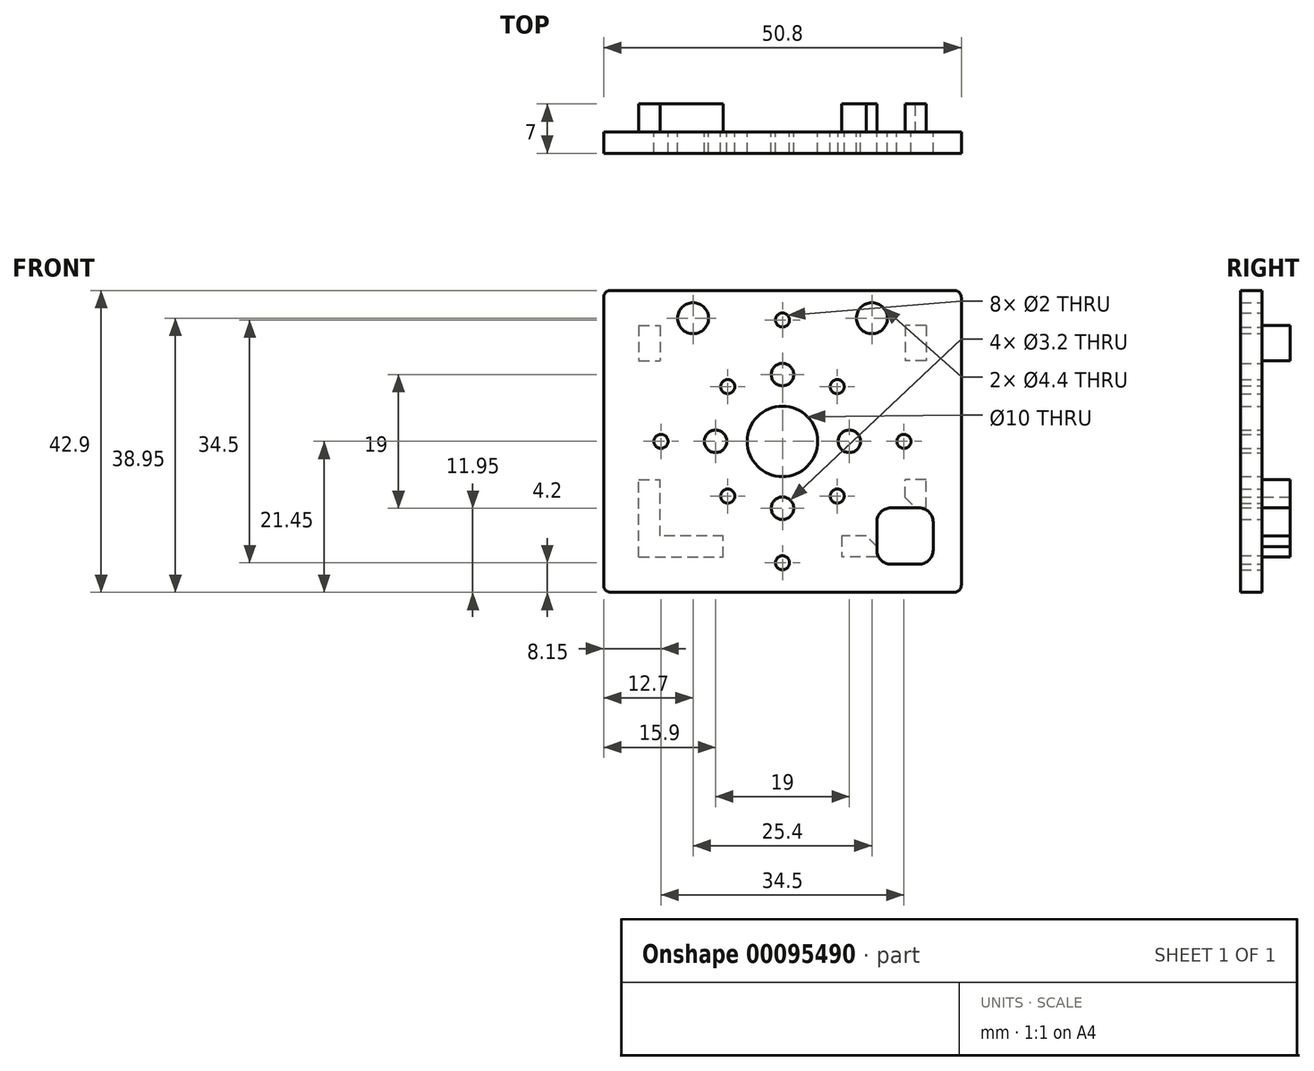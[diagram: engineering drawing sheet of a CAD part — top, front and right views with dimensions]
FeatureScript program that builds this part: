
annotation { "Feature Type Name" : "Feature", "Feature Type Description" : "" }
export const myFeature = defineFeature(function(context is Context, id is Id, definition is map)
    precondition{}
    {
        {
            var Q0;
            Q0=qCreatedBy(makeId("Front.planeOp"),FACE);
            var sketch = newSketch(context, id + "F0", { "sketchPlane" : qUnion([Q0])});
            skLineSegment(sketch, "E0.bottom", {"start": v(25.4, 21.45) * mm, "end": v(-25.4, 21.45) * mm});
            skLineSegment(sketch, "E0.top", {"start": v(25.4, -21.45) * mm, "end": v(-25.4, -21.45) * mm});
            skLineSegment(sketch, "E0.left", {"start": v(25.4, 21.45) * mm, "end": v(25.4, -21.45) * mm});
            skLineSegment(sketch, "E0.right", {"start": v(-25.4, 21.45) * mm, "end": v(-25.4, -21.45) * mm});
            skPoint(sketch, "E0.middle", {"position": v(0, 0) * mm});
            skCircle(sketch, "E1", {"center": v(0, 0) * mm, "radius": 5 * mm});
            skLineSegment(sketch, "E2.bottom", {"start": v(19.4, -17.45) * mm, "end": v(15.4, -17.45) * mm});
            skLineSegment(sketch, "E2.top", {"start": v(19.4, -9.45) * mm, "end": v(15.4, -9.45) * mm});
            skLineSegment(sketch, "E2.left", {"start": v(21.4, -15.45) * mm, "end": v(21.4, -11.45) * mm});
            skLineSegment(sketch, "E2.right", {"start": v(13.4, -15.45) * mm, "end": v(13.4, -11.45) * mm});
            skPoint(sketch, "E3.visualSharp", {"position": v(13.4, -9.45) * mm});
            skArc(sketch, "E3.filletArc", {"start": v(15.4, -9.45) * mm, "mid": v(13.99, -10.04) * mm, "end": v(13.4, -11.45) * mm});
            skPoint(sketch, "E4.visualSharp", {"position": v(21.4, -9.45) * mm});
            skArc(sketch, "E4.filletArc", {"start": v(21.4, -11.45) * mm, "mid": v(20.81, -10.04) * mm, "end": v(19.4, -9.45) * mm});
            skPoint(sketch, "E5.visualSharp", {"position": v(21.4, -17.45) * mm});
            skArc(sketch, "E5.filletArc", {"start": v(19.4, -17.45) * mm, "mid": v(20.81, -16.86) * mm, "end": v(21.4, -15.45) * mm});
            skPoint(sketch, "E6.visualSharp", {"position": v(13.4, -17.45) * mm});
            skArc(sketch, "E6.filletArc", {"start": v(13.4, -15.45) * mm, "mid": v(13.99, -16.86) * mm, "end": v(15.4, -17.45) * mm});
            skCircle(sketch, "E7", {"center": v(0, 17.25) * mm, "radius": 1 * mm});
            skCircle(sketch, "E8", {"center": v(7.78, 7.78) * mm, "radius": 1 * mm});
            skLineSegment(sketch, "E9", {"start": v(0, 0) * mm, "end": v(0, 17.25) * mm, "construction": true});
            skLineSegment(sketch, "E10", {"start": v(0, 0) * mm, "end": v(7.78, 7.78) * mm, "construction": true});
            skCircle(sketch, "E11", {"center": v(-12.7, 17.5) * mm, "radius": 2.2 * mm});
            skCircle(sketch, "E12.MirrorC", {"center": v(12.7, 17.5) * mm, "radius": 2.2 * mm});
            skCircle(sketch, "E13.1.0", {"center": v(-17.25, 0) * mm, "radius": 1 * mm});
            skCircle(sketch, "E13.1.1", {"center": v(-7.78, 7.78) * mm, "radius": 1 * mm});
            skCircle(sketch, "E13.2.0", {"center": v(0, -17.25) * mm, "radius": 1 * mm});
            skCircle(sketch, "E13.2.1", {"center": v(-7.78, -7.78) * mm, "radius": 1 * mm});
            skCircle(sketch, "E13.3.0", {"center": v(17.25, 0) * mm, "radius": 1 * mm});
            skCircle(sketch, "E13.3.1", {"center": v(7.78, -7.78) * mm, "radius": 1 * mm});
            skCircle(sketch, "E14", {"center": v(0, 0) * mm, "radius": 17.25 * mm, "construction": true});
            skCircle(sketch, "E15", {"center": v(0, 0) * mm, "radius": 11 * mm, "construction": true});
            skCircle(sketch, "E16", {"center": v(0, 0) * mm, "radius": 9.5 * mm, "construction": true});
            skCircle(sketch, "E17", {"center": v(9.5, 0) * mm, "radius": 1.6 * mm});
            skCircle(sketch, "E18.1.0", {"center": v(0, 9.5) * mm, "radius": 1.6 * mm});
            skCircle(sketch, "E18.2.0", {"center": v(-9.5, 0) * mm, "radius": 1.6 * mm});
            skCircle(sketch, "E18.3.0", {"center": v(0, -9.5) * mm, "radius": 1.6 * mm});
            skSolve(sketch);
        }
        {
            var Q0;
            Q0=makeQuery(id+"F0.imprint","IMPRINT",FACE,{"disambiguationData":[TD([[makeQuery(id+"F0.imprint","IMPRINT",EDGE,{"derivedFrom":sQuery(id+"F0.wireOp",EDGE,"E0.bottom")}),1.0]])]});
            extrude(context, id + "F1", {"entities" : qUnion([Q0]), "depth" : 3 * mm});
        }
        {
            var Q0;
            Q0=makeQuery(id+"F1.opExtrude","SWEPT_EDGE",EDGE,{"disambiguationData":[OSD([sQuery(id+"F0.wireOp",EDGE,"E0.bottom"),sQuery(id+"F0.wireOp",EDGE,"E0.left")])]});
            var Q1;
            Q1=makeQuery(id+"F1.opExtrude","SWEPT_EDGE",EDGE,{"disambiguationData":[OSD([sQuery(id+"F0.wireOp",EDGE,"E0.top"),sQuery(id+"F0.wireOp",EDGE,"E0.left")])]});
            var Q2;
            Q2=makeQuery(id+"F1.opExtrude","SWEPT_EDGE",EDGE,{"disambiguationData":[OSD([sQuery(id+"F0.wireOp",EDGE,"E0.top"),sQuery(id+"F0.wireOp",EDGE,"E0.right")])]});
            var Q3;
            Q3=makeQuery(id+"F1.opExtrude","SWEPT_EDGE",EDGE,{"disambiguationData":[OSD([sQuery(id+"F0.wireOp",EDGE,"E0.bottom"),sQuery(id+"F0.wireOp",EDGE,"E0.right")])]});
            fillet(context, id + "F2", {"entities" : qUnion([Q0, Q1, Q2, Q3]), "radius" : 1 * mm, "tangentPropagation" : true, "allowEdgeOverflow" : false});
        }
        {
            var Q0;
            Q0=makeQuery(id+"F1.opExtrude","CAP_FACE",FACE,{"disambiguationData":[OSD([sQuery(id+"F0.wireOp",EDGE,"E0.bottom"),sQuery(id+"F0.wireOp",EDGE,"E0.top"),sQuery(id+"F0.wireOp",EDGE,"E0.left"),sQuery(id+"F0.wireOp",EDGE,"E0.right"),sQuery(id+"F0.wireOp",EDGE,"E1"),sQuery(id+"F0.wireOp",EDGE,"E2.bottom"),sQuery(id+"F0.wireOp",EDGE,"E2.top"),sQuery(id+"F0.wireOp",EDGE,"E2.left"),sQuery(id+"F0.wireOp",EDGE,"E2.right"),sQuery(id+"F0.wireOp",EDGE,"E3.filletArc"),sQuery(id+"F0.wireOp",EDGE,"E4.filletArc"),sQuery(id+"F0.wireOp",EDGE,"E5.filletArc"),sQuery(id+"F0.wireOp",EDGE,"E6.filletArc"),sQuery(id+"F0.wireOp",EDGE,"E7"),sQuery(id+"F0.wireOp",EDGE,"E8"),sQuery(id+"F0.wireOp",EDGE,"E11"),sQuery(id+"F0.wireOp",EDGE,"E12.MirrorC"),sQuery(id+"F0.wireOp",EDGE,"E13.1.0"),sQuery(id+"F0.wireOp",EDGE,"E13.1.1"),sQuery(id+"F0.wireOp",EDGE,"E13.2.0"),sQuery(id+"F0.wireOp",EDGE,"E13.2.1"),sQuery(id+"F0.wireOp",EDGE,"E13.3.0"),sQuery(id+"F0.wireOp",EDGE,"E13.3.1")])],"isStart":true});
            var sketch = newSketch(context, id + "F3", { "sketchPlane" : qUnion([Q0])});
            skLineSegment(sketch, "E19.bottom", {"start": v(-20.4, 16.45) * mm, "end": v(-17.4, 16.45) * mm});
            skLineSegment(sketch, "E19.top", {"start": v(-20.4, 11.45) * mm, "end": v(-17.4, 11.45) * mm});
            skLineSegment(sketch, "E19.left", {"start": v(-20.4, 16.45) * mm, "end": v(-20.4, 11.45) * mm});
            skLineSegment(sketch, "E19.right", {"start": v(-17.4, 16.45) * mm, "end": v(-17.4, 11.45) * mm});
            skLineSegment(sketch, "E20.bottom", {"start": v(-20.4, -5.45) * mm, "end": v(-17.4, -5.45) * mm});
            skLineSegment(sketch, "E20.top", {"start": v(-20.4, -9.45) * mm, "end": v(-17.4, -9.45) * mm});
            skLineSegment(sketch, "E20.left", {"start": v(-20.4, -9.45) * mm, "end": v(-20.4, -5.45) * mm});
            skLineSegment(sketch, "E20.right", {"start": v(-17.4, -9.45) * mm, "end": v(-17.4, -5.45) * mm});
            skLineSegment(sketch, "E21.MirrorCS", {"start": v(20.4, 16.45) * mm, "end": v(17.4, 16.45) * mm});
            skLineSegment(sketch, "E22.MirrorCS", {"start": v(20.4, 11.45) * mm, "end": v(17.4, 11.45) * mm});
            skLineSegment(sketch, "E23.MirrorCS", {"start": v(17.4, 16.45) * mm, "end": v(17.4, 11.45) * mm});
            skLineSegment(sketch, "E24.MirrorCS", {"start": v(20.4, 16.45) * mm, "end": v(20.4, 11.45) * mm});
            skLineSegment(sketch, "E25.top", {"start": v(20.4, -5.45) * mm, "end": v(17.4, -5.45) * mm});
            skLineSegment(sketch, "E25.left", {"start": v(20.4, -16.45) * mm, "end": v(20.4, -5.45) * mm});
            skLineSegment(sketch, "E25.right", {"start": v(17.4, -13.45) * mm, "end": v(17.4, -5.45) * mm});
            skLineSegment(sketch, "E26", {"start": v(20.4, -16.45) * mm, "end": v(8.4, -16.45) * mm});
            skLineSegment(sketch, "E27", {"start": v(8.4, -16.45) * mm, "end": v(8.4, -13.45) * mm});
            skLineSegment(sketch, "E28", {"start": v(8.4, -13.45) * mm, "end": v(17.4, -13.45) * mm});
            skLineSegment(sketch, "E29.bottom", {"start": v(-13.4, -13.45) * mm, "end": v(-8.4, -13.45) * mm});
            skLineSegment(sketch, "E29.top", {"start": v(-13.4, -16.45) * mm, "end": v(-8.4, -16.45) * mm});
            skLineSegment(sketch, "E29.left", {"start": v(-13.4, -13.45) * mm, "end": v(-13.4, -16.45) * mm});
            skLineSegment(sketch, "E29.right", {"start": v(-8.4, -13.45) * mm, "end": v(-8.4, -16.45) * mm});
            skSolve(sketch);
        }
        {
            var Q0;
            Q0 = qSketchRegion(id + "F3", true);
            extrude(context, id + "F4", {"entities" : qUnion([Q0]), "operationType" : NewBodyOperationType.ADD, "depth" : 4 * mm});
        }
        {
            var Q0;
            Q0=makeQuery(id+"F4.opExtrude","SWEPT_EDGE",EDGE,{"disambiguationData":[OSD([sQuery(id+"F0.wireOp",EDGE,"E2.right"),sQuery(id+"F3.wireOp",EDGE,"E29.bottom"),sQuery(id+"F3.wireOp",EDGE,"E29.left")])]});
            var Q1;
            Q1=makeQuery(id+"F4.opExtrude","SWEPT_EDGE",EDGE,{"disambiguationData":[OSD([sQuery(id+"F0.wireOp",EDGE,"E2.top"),sQuery(id+"F3.wireOp",EDGE,"E20.top"),sQuery(id+"F3.wireOp",EDGE,"E20.right")])]});
            chamfer(context, id + "F5", {"entities" : qUnion([Q0, Q1]), "width" : 1.5 * mm, "tangentPropagation" : true});
        }
    });
